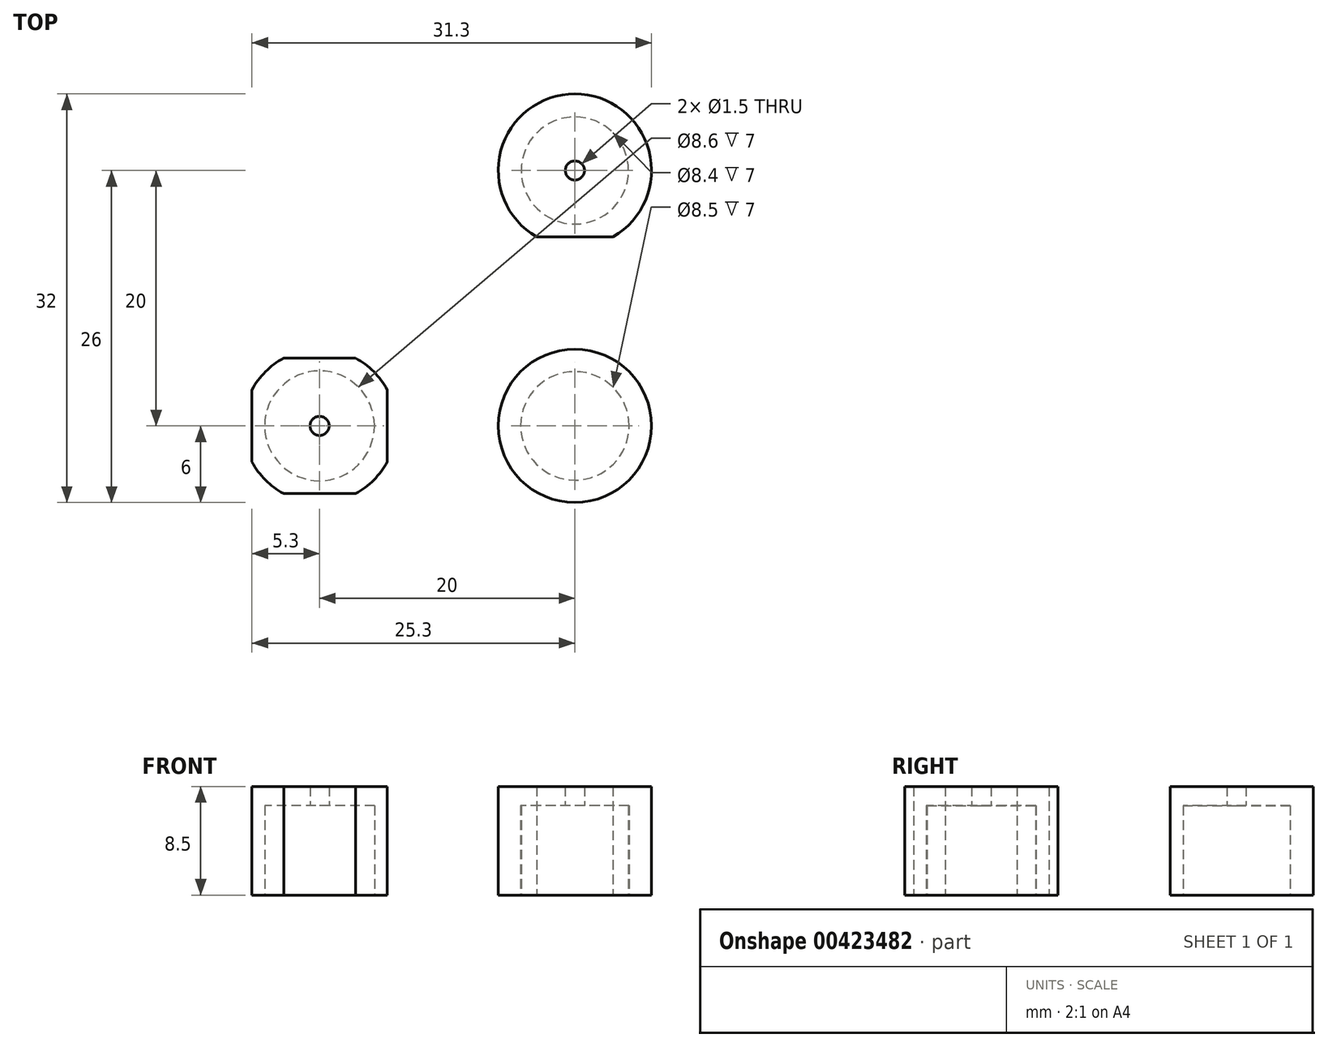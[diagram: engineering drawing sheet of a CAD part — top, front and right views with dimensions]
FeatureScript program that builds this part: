
annotation { "Feature Type Name" : "Feature", "Feature Type Description" : "" }
export const myFeature = defineFeature(function(context is Context, id is Id, definition is map)
    precondition{}
    {
        {
            var Q0;
            Q0=qCreatedBy(makeId("Top.planeOp"),FACE);
            var sketch = newSketch(context, id + "F0", { "sketchPlane" : qUnion([Q0])});
            skLineSegment(sketch, "E0", {"start": v(2.9, -5.25) * mm, "end": v(2.9, -5.25) * mm});
            skCircle(sketch, "E1", {"center": v(0, 0) * mm, "radius": 4.25 * mm});
            skArc(sketch, "E2", {"start": v(-17.19, -5.3) * mm, "mid": v(-15.76, -4.24) * mm, "end": v(-14.7, -2.81) * mm});
            skCircle(sketch, "E3", {"center": v(-20, 0) * mm, "radius": 4.3 * mm});
            skArc(sketch, "E4", {"start": v(3, 14.8) * mm, "mid": v(0, 26) * mm, "end": v(-3, 14.8) * mm});
            skCircle(sketch, "E5", {"center": v(0, 20) * mm, "radius": 4.2 * mm});
            skLineSegment(sketch, "E6", {"start": v(-22.81, -5.3) * mm, "end": v(-17.19, -5.3) * mm});
            skLineSegment(sketch, "E7", {"start": v(-3, 14.8) * mm, "end": v(3, 14.8) * mm});
            skCircle(sketch, "E8", {"center": v(0, 0) * mm, "radius": 6 * mm});
            skLineSegment(sketch, "E9", {"start": v(-25.3, 2.81) * mm, "end": v(-25.3, -2.81) * mm});
            skLineSegment(sketch, "E10", {"start": v(-22.81, 5.3) * mm, "end": v(-17.19, 5.3) * mm});
            skLineSegment(sketch, "E11", {"start": v(-14.7, 2.81) * mm, "end": v(-14.7, -2.81) * mm});
            skArc(sketch, "E12.trimOffspring", {"start": v(-22.81, 5.3) * mm, "mid": v(-24.24, 4.24) * mm, "end": v(-25.3, 2.81) * mm});
            skArc(sketch, "E13.trimOffspring", {"start": v(-25.3, -2.81) * mm, "mid": v(-24.24, -4.24) * mm, "end": v(-22.81, -5.3) * mm});
            skArc(sketch, "E14.trimOffspring", {"start": v(-14.7, 2.81) * mm, "mid": v(-15.76, 4.24) * mm, "end": v(-17.19, 5.3) * mm});
            skSolve(sketch);
        }
        {
            var Q0;
            Q0=makeQuery(id+"F0.imprint","IMPRINT",FACE,{"disambiguationData":[TD([[makeQuery(id+"F0.imprint","IMPRINT",EDGE,{"derivedFrom":sQuery(id+"F0.wireOp",EDGE,"E3")}),1.0]])]});
            var Q1;
            Q1=makeQuery(id+"F0.imprint","IMPRINT",FACE,{"disambiguationData":[TD([[makeQuery(id+"F0.imprint","IMPRINT",EDGE,{"derivedFrom":sQuery(id+"F0.wireOp",EDGE,"E2")}),1.0]])]});
            var Q2;
            Q2=makeQuery(id+"F0.imprint","IMPRINT",FACE,{"disambiguationData":[TD([[makeQuery(id+"F0.imprint","IMPRINT",EDGE,{"derivedFrom":sQuery(id+"F0.wireOp",EDGE,"E0")}),1.0]])]});
            var Q3;
            Q3=makeQuery(id+"F0.imprint","IMPRINT",FACE,{"disambiguationData":[TD([[makeQuery(id+"F0.imprint","IMPRINT",EDGE,{"derivedFrom":sQuery(id+"F0.wireOp",EDGE,"E1")}),1.0]])]});
            var Q4;
            Q4=makeQuery(id+"F0.imprint","IMPRINT",FACE,{"disambiguationData":[TD([[makeQuery(id+"F0.imprint","IMPRINT",EDGE,{"derivedFrom":sQuery(id+"F0.wireOp",EDGE,"E5")}),1.0]])]});
            var Q5;
            Q5=makeQuery(id+"F0.imprint","IMPRINT",FACE,{"disambiguationData":[TD([[makeQuery(id+"F0.imprint","IMPRINT",EDGE,{"derivedFrom":sQuery(id+"F0.wireOp",EDGE,"E4")}),1.0]])]});
            var Q6;
            Q6=makeQuery(id+"F0.imprint","IMPRINT",FACE,{"disambiguationData":[TD([[makeQuery(id+"F0.imprint","IMPRINT",EDGE,{"derivedFrom":sQuery(id+"F0.wireOp",EDGE,"Tjrb3mVH-Yjfx-51If-rg3D-8AJ6jwgc2kGQ")}),1.0]])]});
            var Q7;
            Q7=makeQuery(id+"F0.imprint","IMPRINT",FACE,{"disambiguationData":[TD([[makeQuery(id+"F0.imprint","IMPRINT",EDGE,{"derivedFrom":sQuery(id+"F0.wireOp",EDGE,"u3yj8y9O-qVW9-CNGv-zPkt-jAehiyPjTBoZ")}),1.0]])]});
            var Q8;
            Q8=makeQuery(id+"F0.imprint","IMPRINT",FACE,{"disambiguationData":[TD([[makeQuery(id+"F0.imprint","IMPRINT",EDGE,{"derivedFrom":sQuery(id+"F0.wireOp",EDGE,"l2wQPyHa-nkjW-eFMx-x5oC-QuCLPPrNuH9j")}),1.0]])]});
            var Q9;
            Q9=makeQuery(id+"F0.imprint","IMPRINT",FACE,{"disambiguationData":[TD([[makeQuery(id+"F0.imprint","IMPRINT",EDGE,{"derivedFrom":sQuery(id+"F0.wireOp",EDGE,"u8DZ42rd-vj6L-V0N9-0Bfj-TC6EhqwuHvor")}),1.0]])]});
            var Q10;
            Q10=makeQuery(id+"F0.imprint","IMPRINT",FACE,{"disambiguationData":[TD([[makeQuery(id+"F0.imprint","IMPRINT",EDGE,{"derivedFrom":sQuery(id+"F0.wireOp",EDGE,"E1")}),-1.0]])]});
            extrude(context, id + "F1", {"entities" : qUnion([Q0, Q1, Q2, Q3, Q4, Q5, Q6, Q7, Q8, Q9, Q10]), "depth" : 8.5 * mm, "offsetDistance" : 25 * mm});
        }
        {
            var Q0;
            Q0=makeQuery(id+"F0.imprint","IMPRINT",FACE,{"disambiguationData":[TD([[makeQuery(id+"F0.imprint","IMPRINT",EDGE,{"derivedFrom":sQuery(id+"F0.wireOp",EDGE,"E5")}),1.0]])]});
            var Q1;
            Q1=makeQuery(id+"F0.imprint","IMPRINT",FACE,{"disambiguationData":[TD([[makeQuery(id+"F0.imprint","IMPRINT",EDGE,{"derivedFrom":sQuery(id+"F0.wireOp",EDGE,"E1")}),1.0]])]});
            var Q2;
            Q2=makeQuery(id+"F0.imprint","IMPRINT",FACE,{"disambiguationData":[TD([[makeQuery(id+"F0.imprint","IMPRINT",EDGE,{"derivedFrom":sQuery(id+"F0.wireOp",EDGE,"u8DZ42rd-vj6L-V0N9-0Bfj-TC6EhqwuHvor")}),1.0]])]});
            var Q3;
            Q3=makeQuery(id+"F0.imprint","IMPRINT",FACE,{"disambiguationData":[TD([[makeQuery(id+"F0.imprint","IMPRINT",EDGE,{"derivedFrom":sQuery(id+"F0.wireOp",EDGE,"u3yj8y9O-qVW9-CNGv-zPkt-jAehiyPjTBoZ")}),1.0]])]});
            var Q4;
            Q4=makeQuery(id+"F0.imprint","IMPRINT",FACE,{"disambiguationData":[TD([[makeQuery(id+"F0.imprint","IMPRINT",EDGE,{"derivedFrom":sQuery(id+"F0.wireOp",EDGE,"E3")}),1.0]])]});
            extrude(context, id + "F2", {"entities" : qUnion([Q0, Q1, Q2, Q3, Q4]), "operationType" : NewBodyOperationType.REMOVE, "depth" : 7 * mm, "offsetDistance" : 25 * mm});
        }
        {
            var Q0;
            Q0=sQuery(id+"F0.wireOp",VERTEX,"E2.center");
            var Q1;
            Q1=sQuery(id+"F0.wireOp",VERTEX,"E4.center");
            var Q2;
            Q2=sQuery(id+"F0.wireOp",VERTEX,"l2wQPyHa-nkjW-eFMx-x5oC-QuCLPPrNuH9j.center");
            var Q3;
            Q3=sQuery(id+"F0.wireOp",VERTEX,"Tjrb3mVH-Yjfx-51If-rg3D-8AJ6jwgc2kGQ.center");
            var Q4;
            Q4=sQuery(id+"F0.wireOp",VERTEX,"E0.center");
            var Q5;
            Q5=makeQuery(id+"F1.opExtrude","SWEPT_BODY",BODY,{"disambiguationData":[OSD([sQuery(id+"F0.wireOp",EDGE,"E4"),sQuery(id+"F0.wireOp",EDGE,"E7")])]});
            var Q6;
            Q6=makeQuery(id+"F1.opExtrude","SWEPT_BODY",BODY,{"disambiguationData":[OSD([sQuery(id+"F0.wireOp",EDGE,"l2wQPyHa-nkjW-eFMx-x5oC-QuCLPPrNuH9j"),sQuery(id+"F0.wireOp",EDGE,"w2DFUdFX-gj4U-xVqt-nrid-5r0AiCCyXuio"),sQuery(id+"F0.wireOp",EDGE,"N60cPzdM-s77b-8cVc-WYak-chWfbpj0YfAm"),sQuery(id+"F0.wireOp",EDGE,"fU3bvdqC-qy5F-4W3I-aauP-Cxcj32f6aDpj"),sQuery(id+"F0.wireOp",EDGE,"ca52213a-5835-433f-a3dc-82e9fd238d95.trimOffspring"),sQuery(id+"F0.wireOp",EDGE,"75674eb8-9368-451c-9915-84950260aac1.trimOffspring")])]});
            var Q7;
            Q7=makeQuery(id+"F1.opExtrude","SWEPT_BODY",BODY,{"disambiguationData":[OSD([sQuery(id+"F0.wireOp",EDGE,"Tjrb3mVH-Yjfx-51If-rg3D-8AJ6jwgc2kGQ"),sQuery(id+"F0.wireOp",EDGE,"Bcd0KIhu-THUw-QDvg-8Rgf-wJ69amJ9PNZs"),sQuery(id+"F0.wireOp",EDGE,"PuZCV7FL-GSK9-AYIB-uw1O-eUollInLGQKd"),sQuery(id+"F0.wireOp",EDGE,"0e12c605-ca4c-4400-90bc-660333cefbd7.trimOffspring")])]});
            var Q8;
            Q8=makeQuery(id+"F1.opExtrude","SWEPT_BODY",BODY,{"disambiguationData":[OSD([sQuery(id+"F0.wireOp",EDGE,"E2"),sQuery(id+"F0.wireOp",EDGE,"E6"),sQuery(id+"F0.wireOp",EDGE,"E9"),sQuery(id+"F0.wireOp",EDGE,"E10"),sQuery(id+"F0.wireOp",EDGE,"E11"),sQuery(id+"F0.wireOp",EDGE,"E12.trimOffspring"),sQuery(id+"F0.wireOp",EDGE,"E13.trimOffspring"),sQuery(id+"F0.wireOp",EDGE,"E14.trimOffspring")])]});
            var Q9;
            Q9=makeQuery(id+"F1.opExtrude","SWEPT_BODY",BODY,{"disambiguationData":[OSD([sQuery(id+"F0.wireOp",EDGE,"E8")])]});
            hole(context, id + "F3", {"style" : HoleStyle.SIMPLE, "endStyle" : HoleEndStyle.THROUGH, "oppositeDirection" : true, "holeDiameter" : 1.5 * mm, "isTappedThrough" : true, "tappedDepth" : 12 * mm, "tapClearance" : 3, "locations" : qUnion([Q0, Q1, Q2, Q3, Q4]), "scope" : qUnion([Q5, Q6, Q7, Q8, Q9]), "majorDiameter" : 5 * mm});
        }
    });
